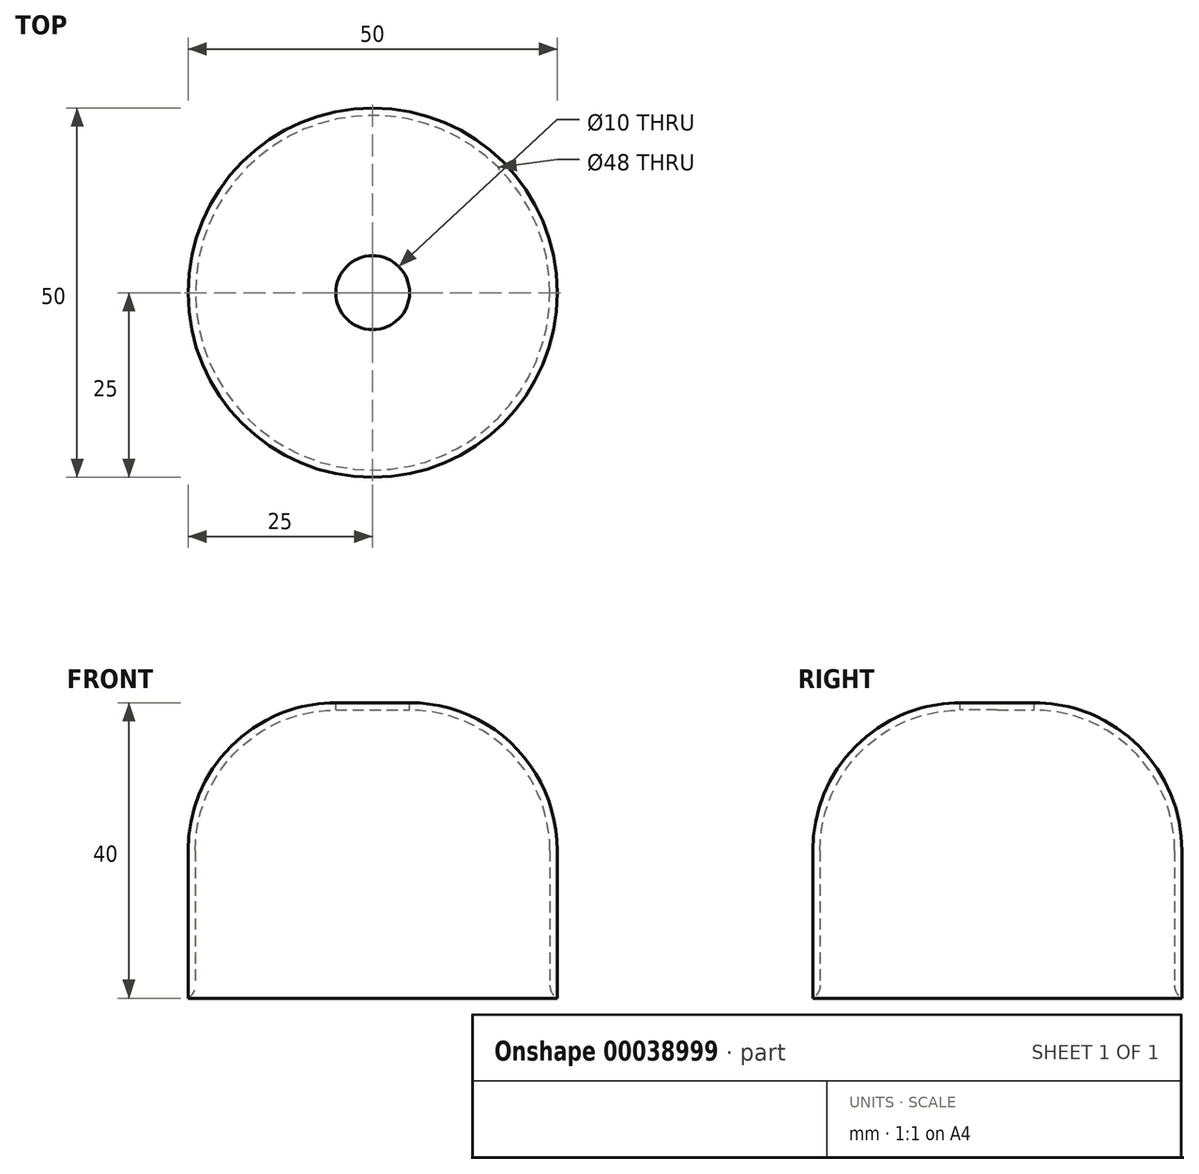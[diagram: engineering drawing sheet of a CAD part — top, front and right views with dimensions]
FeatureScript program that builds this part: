
annotation { "Feature Type Name" : "Feature", "Feature Type Description" : "" }
export const myFeature = defineFeature(function(context is Context, id is Id, definition is map)
    precondition{}
    {
        {
            var Q0;
            Q0=qCreatedBy(makeId("Top.planeOp"),FACE);
            var sketch = newSketch(context, id + "F0", { "sketchPlane" : qUnion([Q0])});
            skCircle(sketch, "E0", {"center": v(0, 0) * mm, "radius": 25 * mm});
            skSolve(sketch);
        }
        {
            var Q0;
            Q0=makeQuery(id+"F0.imprint","IMPRINT",FACE,{"disambiguationData":[TD([[makeQuery(id+"F0.imprint","IMPRINT",EDGE,{"derivedFrom":sQuery(id+"F0.wireOp",EDGE,"E0")}),1.0]])]});
            extrude(context, id + "F1", {"entities" : qUnion([Q0]), "depth" : 40 * mm});
        }
        {
            var Q0;
            Q0=makeQuery(id+"F1.opExtrude","CAP_EDGE",EDGE,{"disambiguationData":[OSD([sQuery(id+"F0.wireOp",EDGE,"E0")])],"isStart":false});
            fillet(context, id + "F2", {"entities" : qUnion([Q0]), "radius" : 20 * mm, "tangentPropagation" : true, "allowEdgeOverflow" : false});
        }
        {
            var Q0;
            Q0=makeQuery(id+"F1.opExtrude","CAP_FACE",FACE,{"disambiguationData":[OSD([sQuery(id+"F0.wireOp",EDGE,"E0")])],"isStart":false});
            var Q1;
            Q1=makeQuery(id+"F1.opExtrude","CAP_FACE",FACE,{"disambiguationData":[OSD([sQuery(id+"F0.wireOp",EDGE,"E0")])],"isStart":true});
            shell(context, id + "F3", {"entities" : qUnion([Q0, Q1]), "thickness" : 1 * mm});
        }
        {
            var Q0;
            {var subQ0=sQuery(id+"F0.wireOp",EDGE,"E0");Q0=makeQuery(id+"F3.opShell","OFFSET_EDGE",EDGE,{"disambiguationData":[OSD([subQ0]),TDD([makeQuery(id+"F1.opExtrude","CAP_EDGE",EDGE,{"disambiguationData":[OSD([subQ0])],"isStart":true})])]});}
            fillet(context, id + "F4", {"entities" : qUnion([Q0]), "radius" : 2 * mm, "tangentPropagation" : true, "allowEdgeOverflow" : false});
        }
    });
